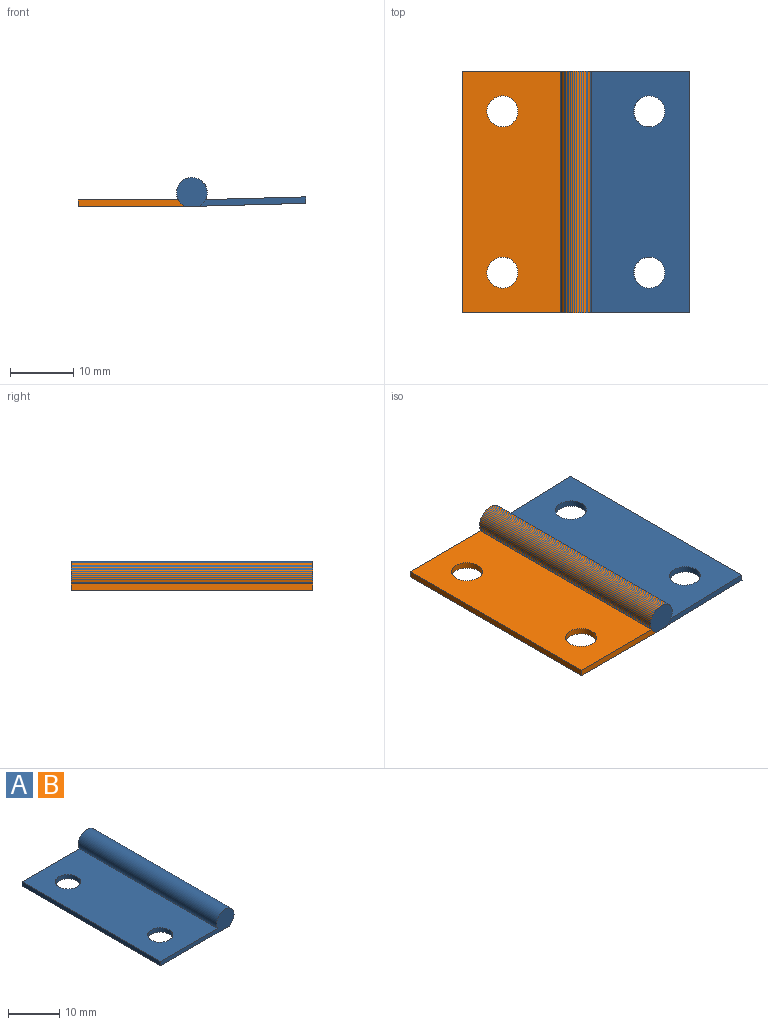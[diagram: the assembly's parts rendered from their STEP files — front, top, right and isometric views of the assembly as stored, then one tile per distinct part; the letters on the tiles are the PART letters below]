
ASSEMBLY  parts=2 mates=1
PART A: 8 faces, bbox 20.3x38.1x4.6 mm
  f0: plane 38.1x1.02mm, normal (-1,0,0), area 38.7mm2, adj f1,f3,f4,f5
  f1: plane 38.1x18.98mm, normal (0,0,-1), area 685.8mm2, adj f0,f2,f4,f5,f6,f7
  f2: cylinder r=2.41mm len=38.1mm, axis (0,1,0), area 436mm2, adj f1,f3,f4,f5
  f3: plane 38.1x15.78mm, normal (0,0,1), area 563.7mm2, adj f0,f2,f4,f5,f6,f7
  f4: plane 20.32x4.57mm, normal (0,-1,0), area 34.4mm2, adj f0,f1,f2,f3
  f5: plane 20.32x4.57mm, normal (0,1,0), area 34.4mm2, adj f0,f1,f2,f3
  f6: cylinder r=2.44mm len=4.89mm, axis (0,0,1), area 15.6mm2, adj f1,f3
  f7: cylinder r=2.44mm len=4.89mm, axis (0,0,1), area 15.6mm2, adj f1,f3
PART B: same geometry as A
PLACE A rot(axis=(0.01,0,-1),180deg) t=(52.95,-12.88,0.94)mm
PLACE B t=(17.08,25.22,0.45)mm fixed
MATE revolute A.f2 <-> B.f2  axis (0,1,0) through (34.99,25.22,2.61)mm
